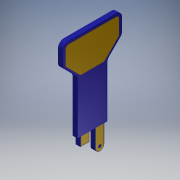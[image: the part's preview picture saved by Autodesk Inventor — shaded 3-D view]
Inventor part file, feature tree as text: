
AUTODESK INVENTOR PART (.ipt)
format: ipt  version: 2016 (Build 200138000, 138)  size: 249,856 bytes
history: native  units: mm
features: other x4, sketch x4, extrude x2, mirror x1, fillet x1
ambient origin geometry x8: Origin, YZ Plane, XZ Plane, XY Plane, X Axis, Y Axis, Z Axis, Center Point
bodies: Solid1 (feature_tree)
feature tree (12):
  extrude  "Extrusion1"  Depth=3.0mm
  mirror  "Mirror1"
  fillet  "Fillet1"  Radius=1.0mm
  extrude  "Extrusion2"  Depth=30.0mm
  other  "Decal1"
  other  "Decal2"
  sketch  "Sketch1"  dims[d0=1.0mm d1=3.0mm d2=1.0mm]
  sketch  "Sketch2"  dims[d3=3.0mm d4=30.0mm]
  sketch  "Sketch3"  dims[d5=7.0mm]
  other  "Image1"
  sketch  "Sketch4"  dims[d6=45.0deg d7=10.0mm d8=1.6mm d9=0.0mm d10=2.0mm d11=3.0mm d12=3.0mm d13=1.0mm d14=1.6mm d15=0.0mm d17=1.5mm d18=1.5mm d20=1.5mm]
  other  "Image2"
